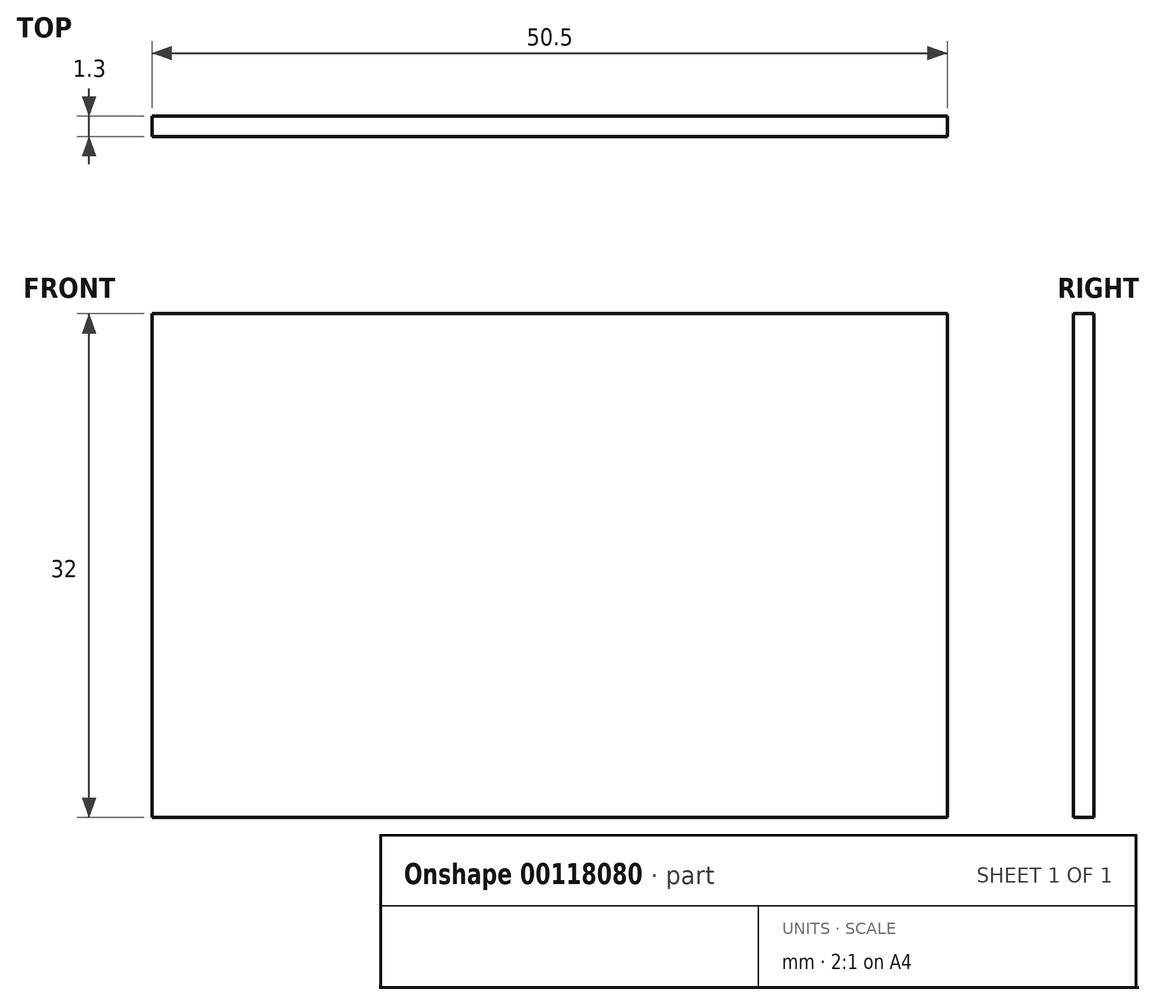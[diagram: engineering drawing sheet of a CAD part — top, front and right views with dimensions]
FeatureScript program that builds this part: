
annotation { "Feature Type Name" : "Feature", "Feature Type Description" : "" }
export const myFeature = defineFeature(function(context is Context, id is Id, definition is map)
    precondition{}
    {
        {
            var Q0;
            Q0=qCreatedBy(makeId("Front.planeOp"),FACE);
            var sketch = newSketch(context, id + "F0", { "sketchPlane" : qUnion([Q0])});
            skLineSegment(sketch, "E0.bottom", {"start": v(25.25, 0) * mm, "end": v(-25.25, 0) * mm});
            skLineSegment(sketch, "E0.top", {"start": v(25.25, 32) * mm, "end": v(-25.25, 32) * mm});
            skLineSegment(sketch, "E0.left", {"start": v(25.25, 0) * mm, "end": v(25.25, 32) * mm});
            skLineSegment(sketch, "E0.right", {"start": v(-25.25, 0) * mm, "end": v(-25.25, 32) * mm});
            skPoint(sketch, "E0.middle", {"position": v(0, 16) * mm});
            skSolve(sketch);
        }
        {
            var Q0;
            Q0=makeQuery(id+"F0.imprint","IMPRINT",FACE,{"disambiguationData":[TD([[makeQuery(id+"F0.imprint","IMPRINT",EDGE,{"derivedFrom":sQuery(id+"F0.wireOp",EDGE,"E0.bottom")}),-1.0]])]});
            extrude(context, id + "F1", {"entities" : qUnion([Q0]), "depth" : 1.3 * mm});
        }
    });
